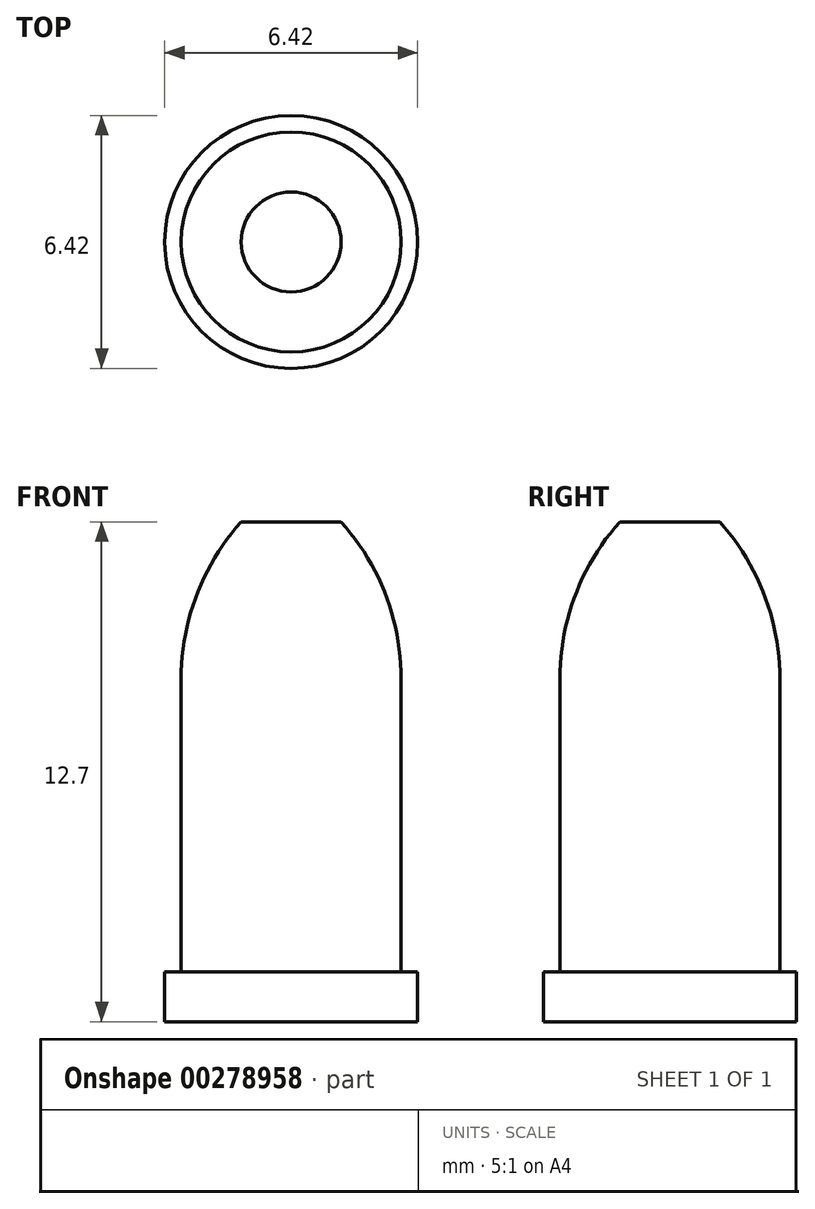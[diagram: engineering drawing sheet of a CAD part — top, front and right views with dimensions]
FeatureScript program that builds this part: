
annotation { "Feature Type Name" : "Feature", "Feature Type Description" : "" }
export const myFeature = defineFeature(function(context is Context, id is Id, definition is map)
    precondition{}
    {
        {
            var Q0;
            Q0=qCreatedBy(makeId("Front.planeOp"),FACE);
            var sketch = newSketch(context, id + "F0", { "sketchPlane" : qUnion([Q0])});
            skLineSegment(sketch, "E0", {"start": v(0, 0) * mm, "end": v(3.21, 0) * mm});
            skLineSegment(sketch, "E1", {"start": v(3.21, 0) * mm, "end": v(3.21, 1.27) * mm});
            skLineSegment(sketch, "E2", {"start": v(-1.27, 12.7) * mm, "end": v(0, 12.7) * mm});
            skLineSegment(sketch, "E3", {"start": v(3.21, 1.27) * mm, "end": v(2.8, 1.27) * mm});
            skLineSegment(sketch, "E4", {"start": v(2.8, 1.27) * mm, "end": v(2.8, 8.7) * mm});
            skLineSegment(sketch, "E5.MirrorCS", {"start": v(-3.21, 1.27) * mm, "end": v(-2.8, 1.27) * mm});
            skLineSegment(sketch, "E6.MirrorCS", {"start": v(1.27, 12.7) * mm, "end": v(0, 12.7) * mm});
            skLineSegment(sketch, "E7.MirrorCS", {"start": v(-3.21, 0) * mm, "end": v(-3.21, 1.27) * mm});
            skLineSegment(sketch, "E8.MirrorCS", {"start": v(0, 0) * mm, "end": v(-3.21, 0) * mm});
            skLineSegment(sketch, "E9.MirrorCS", {"start": v(-2.8, 1.27) * mm, "end": v(-2.8, 8.7) * mm});
            skArc(sketch, "E10", {"start": v(-1.27, 12.7) * mm, "mid": v(-2.4, 10.84) * mm, "end": v(-2.8, 8.7) * mm});
            skArc(sketch, "E11", {"start": v(2.8, 8.7) * mm, "mid": v(2.4, 10.84) * mm, "end": v(1.27, 12.7) * mm});
            skLineSegment(sketch, "E12", {"start": v(0, 0) * mm, "end": v(0, 12.7) * mm});
            skSolve(sketch);
        }
        {
            var Q0;
            Q0=makeQuery(id+"F0.imprint","IMPRINT",FACE,{"disambiguationData":[TD([[makeQuery(id+"F0.imprint","IMPRINT",EDGE,{"derivedFrom":sQuery(id+"F0.wireOp",EDGE,"E0")}),1.0]])]});
            var Q1;
            Q1=sQuery(id+"F0.wireOp",EDGE,"E12");
            revolve(context, id + "F1", {"entities" : qUnion([Q0]), "axis" : qUnion([Q1]), "revolveType" : RevolveType.FULL});
        }
    });
